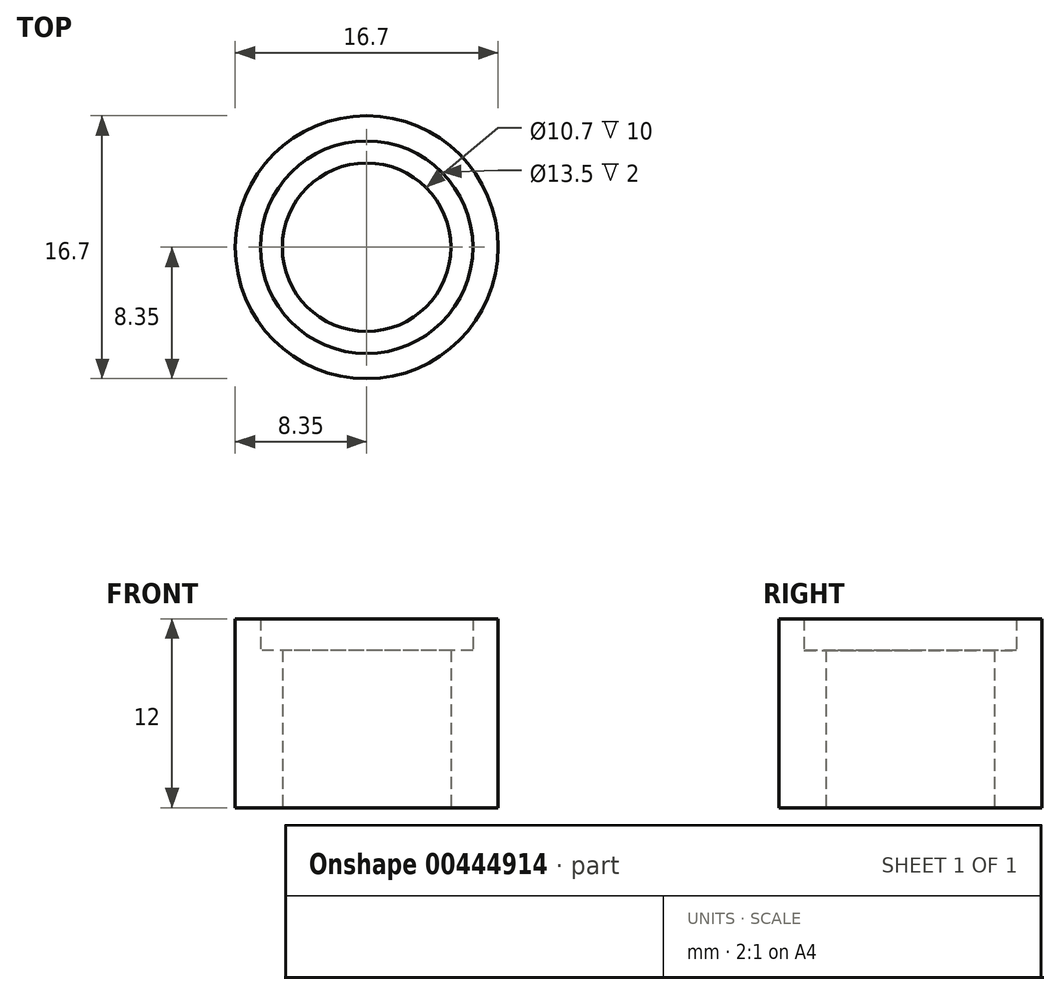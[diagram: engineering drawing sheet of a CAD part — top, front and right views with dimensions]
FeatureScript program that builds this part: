
annotation { "Feature Type Name" : "Feature", "Feature Type Description" : "" }
export const myFeature = defineFeature(function(context is Context, id is Id, definition is map)
    precondition{}
    {
        {
            var Q0;
            Q0=qCreatedBy(makeId("Top.planeOp"),FACE);
            var sketch = newSketch(context, id + "F0", { "sketchPlane" : qUnion([Q0])});
            skCircle(sketch, "E0", {"center": v(0, 0) * mm, "radius": 5.35 * mm});
            skCircle(sketch, "E1.0", {"center": v(0, 0) * mm, "radius": 8.35 * mm});
            skSolve(sketch);
        }
        {
            var Q0;
            Q0=makeQuery(id+"F0.imprint","IMPRINT",FACE,{"disambiguationData":[TD([[makeQuery(id+"F0.imprint","IMPRINT",EDGE,{"derivedFrom":sQuery(id+"F0.wireOp",EDGE,"E0")}),-1.0]])]});
            extrude(context, id + "F1", {"entities" : qUnion([Q0]), "depth" : 10 * mm, "offsetDistance" : 25 * mm});
        }
        {
            var Q0;
            Q0=makeQuery(id+"F1.opExtrude","CAP_FACE",FACE,{"disambiguationData":[OSD([sQuery(id+"F0.wireOp",EDGE,"E0"),sQuery(id+"F0.wireOp",EDGE,"E1.0")])],"isStart":false});
            var sketch = newSketch(context, id + "F2", { "sketchPlane" : qUnion([Q0])});
            skCircle(sketch, "E2", {"center": v(0, 0) * mm, "radius": 6.75 * mm});
            skCircle(sketch, "E3.0", {"center": v(0, 0) * mm, "radius": 8.35 * mm});
            skSolve(sketch);
        }
        {
            var Q0;
            Q0=makeQuery(id+"F2.imprint","IMPRINT",FACE,{"disambiguationData":[TD([[makeQuery(id+"F2.imprint","IMPRINT",EDGE,{"derivedFrom":sQuery(id+"F2.wireOp",EDGE,"E2")}),-1.0]])]});
            extrude(context, id + "F3", {"entities" : qUnion([Q0]), "operationType" : NewBodyOperationType.ADD, "depth" : 2 * mm, "offsetDistance" : 25 * mm});
        }
    });
